# Revit family: QF_Vollrath_36491_cat
name_source: partatom
category: Specialty Equipment
revit_build: Autodesk Revit 2016 (Build: 20151007_0715(x64)
units: mm (PartAtom-declared; Revit-internal decimal feet)

## family parameters
Always vertical = Yes
Cut with Voids When Loaded = No
OmniClass Number = 23.40.40.14.14
OmniClass Title = Food Preparation Equipment
Part Type = Normal
Room Calculation Point = No
Round Connector Dimension = Use Diameter
Shared = No
Work Plane-Based = No

## types (1)
- QF_Vollrath_36491_cat
    Apparent Power = 588 VA
    Assembly Code = E1090320
    CSI MasterFormat = 11 42 00
    Conn Plug = NEMA 5-15P
    Description = Refrigerated Cold Pan Drop-In
    Display Width B = 3' - 1 1/2"
    FL Amps = 5 A
    HP = 1/4
    Half Display Width = 1' - 6 3/4"
    Indirect Waste Size = 1"
    Manufacturer = Vollrath
    Model = -
    Non Remote = Yes
    Overall Width A = 4' - 5 1/2"
    Phase = 1
    Remote = No
    URL = www.vollrathco.com
    Volts = 120 V
    Waste Water Discharge Temperature = -460 °F
    Weight in Pounds = 0

## geometry (parser evidence)
native form markers: Blend x18, Sweep x2
no freeform markers — native parametric forms only
